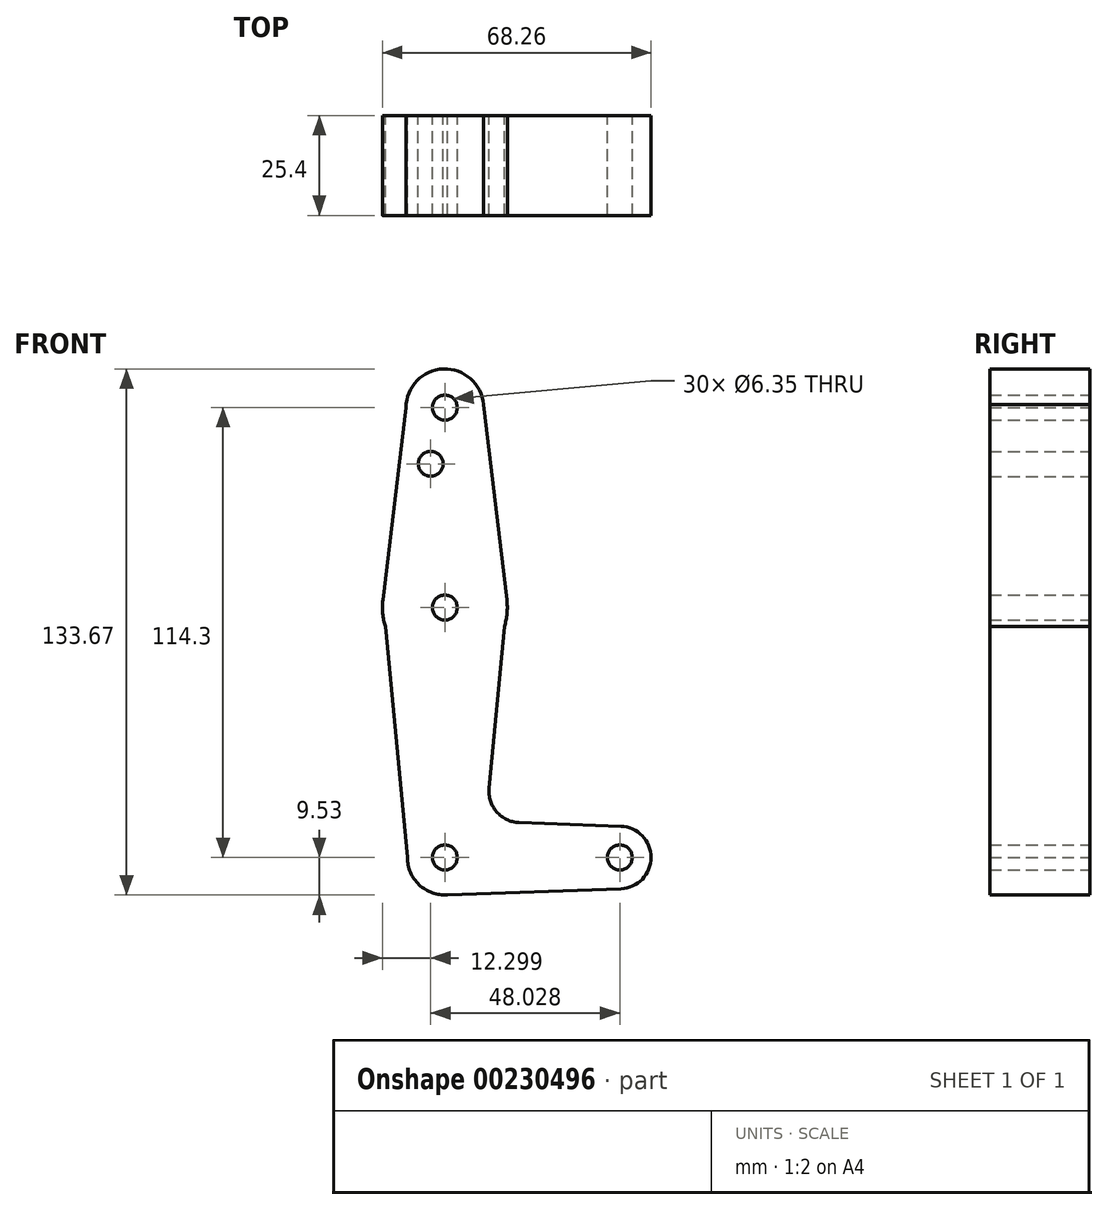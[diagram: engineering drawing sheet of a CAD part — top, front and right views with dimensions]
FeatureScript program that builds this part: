
annotation { "Feature Type Name" : "Feature", "Feature Type Description" : "" }
export const myFeature = defineFeature(function(context is Context, id is Id, definition is map)
    precondition{}
    {
        {
            var Q0;
            Q0=qCreatedBy(makeId("Front.planeOp"),FACE);
            var sketch = newSketch(context, id + "F0", { "sketchPlane" : qUnion([Q0])});
            skLineSegment(sketch, "E0", {"start": v(-64.41, 114.3) * mm, "end": v(-64.41, 63.5) * mm});
            skLineSegment(sketch, "E1", {"start": v(-64.41, 114.3) * mm, "end": v(-64.41, 0) * mm});
            skLineSegment(sketch, "E2", {"start": v(-64.41, 0) * mm, "end": v(-19.96, 0) * mm});
            skCircle(sketch, "E3", {"center": v(-64.41, 63.5) * mm, "radius": 15.88 * mm});
            skCircle(sketch, "E4", {"center": v(-64.41, 114.3) * mm, "radius": 9.84 * mm});
            skCircle(sketch, "E5", {"center": v(-64.41, 0) * mm, "radius": 9.53 * mm});
            skCircle(sketch, "E6", {"center": v(-19.96, 0) * mm, "radius": 7.94 * mm});
            skLineSegment(sketch, "E7", {"start": v(-74.25, 114.3) * mm, "end": v(-80.17, 65.4) * mm});
            skLineSegment(sketch, "E8", {"start": v(-80.17, 65.4) * mm, "end": v(-73.94, 0) * mm});
            skLineSegment(sketch, "E9", {"start": v(-64.41, -9.53) * mm, "end": v(-19.68, -7.93) * mm});
            skLineSegment(sketch, "E10", {"start": v(-45.56, 8.88) * mm, "end": v(-19.67, 7.93) * mm});
            skCircle(sketch, "E11", {"center": v(-64.41, 114.3) * mm, "radius": 3.18 * mm});
            skArc(sketch, "E12.filletArc", {"start": v(-53.18, 17.58) * mm, "mid": v(-51.24, 11.59) * mm, "end": v(-45.56, 8.88) * mm});
            skCircle(sketch, "E13", {"center": v(-68, 100.03) * mm, "radius": 3.18 * mm});
            skCircle(sketch, "E14", {"center": v(-64.41, 63.5) * mm, "radius": 3.18 * mm});
            skCircle(sketch, "E15", {"center": v(-64.41, 0) * mm, "radius": 3.18 * mm});
            skCircle(sketch, "E16", {"center": v(-19.96, 0) * mm, "radius": 3.18 * mm});
            skLineSegment(sketch, "E17", {"start": v(-48.65, 65.4) * mm, "end": v(-53.18, 17.58) * mm});
            skLineSegment(sketch, "E18", {"start": v(-54.6, 115.1) * mm, "end": v(-48.65, 65.4) * mm});
            skSolve(sketch);
        }
        {
            var Q0;
            Q0 = qSketchRegion(id + "F0", true);
            var Q1;
            {var subQ0=sQuery(id+"F0.wireOp",EDGE,"E5");var subQ1=sQuery(id+"F0.wireOp",EDGE,"E1");var subQ2=makeQuery(id+"F0.imprint","INTERSECT",VERTEX,{"derivedFrom":[subQ1,subQ0]});Q1=makeQuery(id+"F0.imprint","IMPRINT",FACE,{"disambiguationData":[TD([[makeQuery(id+"F0.imprint","IMPRINT",EDGE,{"disambiguationData":[TD([[subQ2,-1.0]])],"derivedFrom":subQ1}),1.0]])]});}
            extrude(context, id + "F1", {"entities" : qUnion([Q0, Q1]), "depth" : 25.4 * mm});
        }
    });
